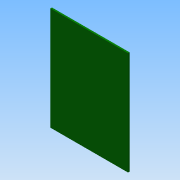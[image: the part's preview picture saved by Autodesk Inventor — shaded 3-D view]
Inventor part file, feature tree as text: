
AUTODESK INVENTOR PART (.ipt)
format: ipt  version: 2014 (Build 180170000, 170)  size: 74,240 bytes
history: native  units: in
note: dims shown in document units (in); Inventor stores cm internally (conversion verified against a paired STEP export)
features: reference x4, extrude x1, sketch x1
ambient origin geometry x8: Origin, YZ Plane, XZ Plane, XY Plane, X Axis, Y Axis, Z Axis, Center Point
bodies: Solid1 (feature_tree)
feature tree (6):
  extrude  "Extrusion1"  Depth=0.1in TaperAngle=0.0deg
  sketch  "Sketch1"  dims[d1=0.5in d2=0.1in d3=0.0in d4=0.5in]
  reference  "Reference1"
  reference  "Reference3"
  reference  "Reference4"
  reference  "Reference5"
